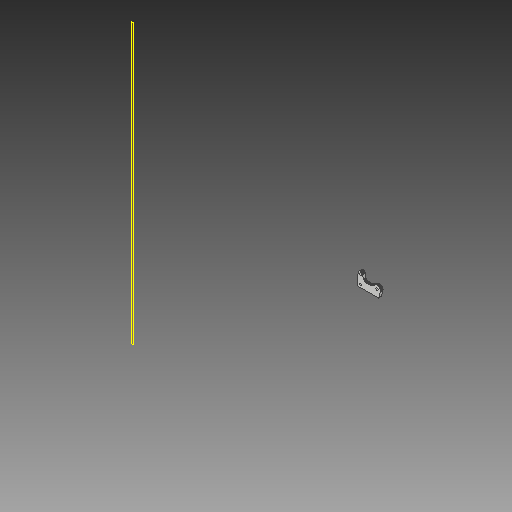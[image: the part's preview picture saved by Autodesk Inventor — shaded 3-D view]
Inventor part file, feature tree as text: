
AUTODESK INVENTOR PART (.ipt)
format: ipt  version: 2017 (Build 210142000, 142)  size: 305,664 bytes
history: native  units: mm
features: other x3, sketch x2, plane x1
ambient origin geometry x8: Origin, YZ Plane, XZ Plane, XY Plane, X Axis, Y Axis, Z Axis, Center Point
bodies: Solid1 (feature_tree)
feature tree (6):
  other  "X-Idler_MIR.ipt"
  other  "Solid1::X-Idler_MIR.ipt"
  other  "TaggingFeature1"
  sketch  "Sketch1"  dims[d0=10.0mm]
  sketch  "Sketch2"
  plane  "Work Plane1"
